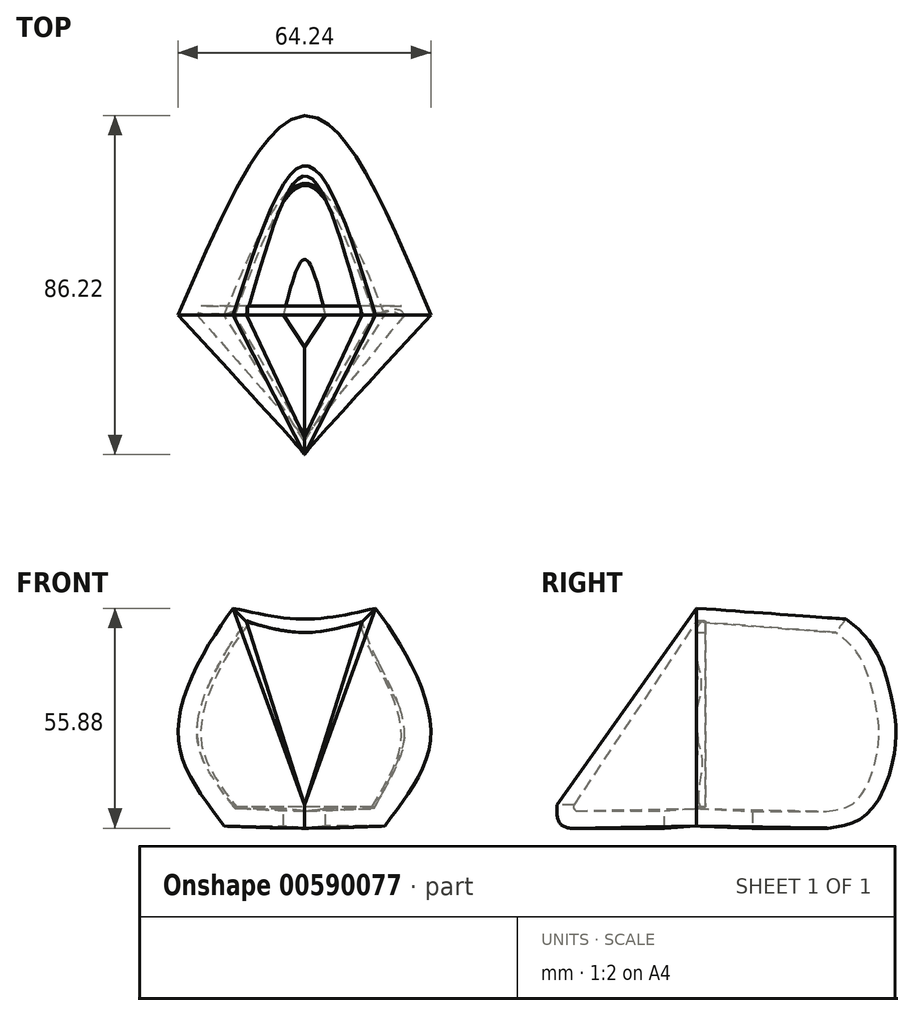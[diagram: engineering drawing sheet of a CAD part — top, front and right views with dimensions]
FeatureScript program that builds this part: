
annotation { "Feature Type Name" : "Feature", "Feature Type Description" : "" }
export const myFeature = defineFeature(function(context is Context, id is Id, definition is map)
    precondition{}
    {
        {
            var Q0;
            Q0=qCreatedBy(makeId("Right.planeOp"),FACE);
            var sketch = newSketch(context, id + "F0", { "sketchPlane" : qUnion([Q0])});
            skLineSegment(sketch, "E0", {"start": v(0, 0) * mm, "end": v(0, 26.93) * mm, "construction": true});
            skLineSegment(sketch, "E1", {"start": v(14.1, 0) * mm, "end": v(33.38, 0) * mm});
            skFitSpline(sketch, "E2", {"points": [v(33.38, 0) * mm, v(40.37, 1.65) * mm, v(46.58, 7.95) * mm, v(50.49, 20.86) * mm, v(49.98, 30.7) * mm, v(45.22, 45.65) * mm, v(37.92, 53.12) * mm], "startDerivative": vector(53.03, 6.53) * mm, "endDerivative": vector(-48.37, 37.27) * mm});
            skFitSpline(sketch, "E3.0", {"points": [v(32.85, 4.29) * mm, v(33.4, 4.35) * mm, v(34.46, 4.48) * mm, v(35.88, 4.71) * mm, v(37.12, 5) * mm, v(38, 5.3) * mm, v(38.61, 5.59) * mm, v(39.07, 5.84) * mm, v(39.52, 6.14) * mm, v(40.13, 6.6) * mm, v(40.88, 7.31) * mm, v(41.78, 8.39) * mm, v(42.5, 9.48) * mm, v(43.05, 10.48) * mm, v(43.58, 11.59) * mm, v(44.22, 13.11) * mm, v(44.89, 15.1) * mm, v(45.45, 17.14) * mm, v(45.88, 19.16) * mm, v(46.13, 20.75) * mm, v(46.26, 21.92) * mm, v(46.35, 23.02) * mm, v(46.38, 24.3) * mm, v(46.3, 25.84) * mm, v(46.13, 27.48) * mm, v(45.9, 29) * mm, v(45.65, 30.36) * mm, v(45.38, 31.8) * mm, v(44.82, 34.41) * mm, v(44, 37.52) * mm, v(43.12, 40.03) * mm, v(42.57, 41.35) * mm, v(42.15, 42.27) * mm, v(41.71, 43.1) * mm, v(41.28, 43.84) * mm, v(40.81, 44.53) * mm, v(40.16, 45.38) * mm, v(39.28, 46.36) * mm, v(37.7, 47.84) * mm, v(36.3, 48.92) * mm, v(35.28, 49.7) * mm]});
            skLineSegment(sketch, "E4", {"start": v(35.28, 49.7) * mm, "end": v(37.92, 53.12) * mm});
            skLineSegment(sketch, "E5", {"start": v(32.9, 4.3) * mm, "end": v(14.1, 4.3) * mm});
            skLineSegment(sketch, "E6", {"start": v(14.1, 0) * mm, "end": v(14.1, 4.3) * mm});
            skSolve(sketch);
        }
        {
            var Q0;
            Q0=qCreatedBy(makeId("Front.planeOp"),FACE);
            var sketch = newSketch(context, id + "F1", { "sketchPlane" : qUnion([Q0])});
            skLineSegment(sketch, "E7", {"start": v(-17.7, 4.97) * mm, "end": v(-5.36, 4.97) * mm});
            skLineSegment(sketch, "E8", {"start": v(-20.45, 0.52) * mm, "end": v(-5.36, 0.52) * mm});
            skLineSegment(sketch, "E9", {"start": v(-5.36, 0.52) * mm, "end": v(-5.36, 4.97) * mm});
            skFitSpline(sketch, "E10", {"points": [v(-20.45, 0.52) * mm, v(-32.12, 24.06) * mm, v(-18.1, 55.88) * mm], "startDerivative": vector(-32.93, 46.47) * mm, "endDerivative": vector(34.01, 45.62) * mm});
            skFitSpline(sketch, "E11.0", {"points": [v(-16.51, 3.31) * mm, v(-17.95, 5.34) * mm, v(-20.15, 8.25) * mm, v(-22.78, 12.01) * mm, v(-24.49, 14.79) * mm, v(-25.85, 17.52) * mm, v(-26.64, 19.76) * mm, v(-27.05, 21.56) * mm, v(-27.21, 22.69) * mm, v(-27.28, 23.6) * mm, v(-27.3, 24.3) * mm, v(-27.29, 25.02) * mm, v(-27.23, 26.01) * mm, v(-27.07, 27.32) * mm, v(-26.65, 29.52) * mm, v(-25.82, 32.43) * mm, v(-24.4, 36.08) * mm, v(-22.06, 41) * mm, v(-18.52, 47) * mm, v(-15.59, 51.17) * mm, v(-14.23, 53) * mm]});
            skLineSegment(sketch, "E12", {"start": v(-18.1, 55.88) * mm, "end": v(-14.66, 52.41) * mm});
            skLineSegment(sketch, "E13.MirrorCS", {"start": v(17.7, 4.97) * mm, "end": v(5.36, 4.97) * mm});
            skLineSegment(sketch, "E14.MirrorCS", {"start": v(20.45, 0.52) * mm, "end": v(5.36, 0.52) * mm});
            skFitSpline(sketch, "E15.MirrorCS", {"points": [v(20.45, 0.52) * mm, v(32.12, 24.06) * mm, v(18.1, 55.88) * mm], "startDerivative": vector(32.93, 46.47) * mm, "endDerivative": vector(-34.01, 45.62) * mm});
            skLineSegment(sketch, "E16.MirrorCS", {"start": v(18.1, 55.88) * mm, "end": v(14.66, 52.41) * mm});
            skLineSegment(sketch, "E17.MirrorCS", {"start": v(5.36, 0.52) * mm, "end": v(5.36, 4.97) * mm});
            skFitSpline(sketch, "E18", {"points": [v(17.7, 4.97) * mm, v(21.14, 11.3) * mm, v(25.22, 21.15) * mm, v(23.52, 32.53) * mm, v(17.7, 44.42) * mm, v(14.66, 52.41) * mm], "startDerivative": vector(19, 35.34) * mm, "endDerivative": vector(-13.78, 41.56) * mm});
            skSolve(sketch);
        }
        {
            var Q0;
            Q0=qCreatedBy(makeId("Right.planeOp"),FACE);
            var sketch = newSketch(context, id + "F2", { "sketchPlane" : qUnion([Q0])});
            skLineSegment(sketch, "E19", {"start": v(-8.23, 0) * mm, "end": v(-32.12, 0) * mm});
            skFitSpline(sketch, "E20", {"points": [v(-32.12, 0) * mm, v(-34.22, 0.72) * mm, v(-35.36, 2.7) * mm, v(-35.48, 5.94) * mm], "startDerivative": vector(-7.4, 1.41) * mm, "endDerivative": vector(0.4, 9.03) * mm});
            skLineSegment(sketch, "E21", {"start": v(-8.23, 0) * mm, "end": v(-8.23, 4.44) * mm});
            skLineSegment(sketch, "E22", {"start": v(-30.68, 4.44) * mm, "end": v(-8.23, 4.44) * mm});
            skFitSpline(sketch, "E23", {"points": [v(-30.68, 4.44) * mm, v(-31.16, 5.1) * mm, v(-31.1, 5.94) * mm], "startDerivative": vector(-1.24, 1.25) * mm, "endDerivative": vector(0.4, 1.75) * mm});
            skLineSegment(sketch, "E24", {"start": v(-31.1, 5.94) * mm, "end": v(-35.48, 5.94) * mm});
            skSolve(sketch);
        }
        {
            var Q0;
            Q0=makeQuery(id+"F2.imprint","IMPRINT",FACE,{"disambiguationData":[TD([[makeQuery(id+"F2.imprint","IMPRINT",EDGE,{"derivedFrom":sQuery(id+"F2.wireOp",EDGE,"E19")}),-1.0]])]});
            var Q1;
            Q1=makeQuery(id+"F1.imprint","IMPRINT",FACE,{"disambiguationData":[TD([[makeQuery(id+"F1.imprint","IMPRINT",EDGE,{"derivedFrom":sQuery(id+"F1.wireOp",EDGE,"E13.MirrorCS")}),1.0]])]});
            loft(context, id + "F3", {"sheetProfilesArray" : [{ "sheetProfileEntities" : qUnion([Q0]) }, { "sheetProfileEntities" : qUnion([Q1]) }]});
        }
        {
            var Q1;
            Q1=makeQuery(id+"F3.opLoft","CAP_FACE",FACE,{"disambiguationData":[OSD([makeQuery(id+"F2.imprint","IMPRINT",FACE,{"disambiguationData":[TD([[makeQuery(id+"F2.imprint","IMPRINT",EDGE,{"derivedFrom":sQuery(id+"F2.wireOp",EDGE,"E19")}),-1.0]])]})])],"isStart":true});
            var Q2;
            Q2=makeQuery(id+"F1.imprint","IMPRINT",FACE,{"disambiguationData":[TD([[makeQuery(id+"F1.imprint","IMPRINT",EDGE,{"derivedFrom":sQuery(id+"F1.wireOp",EDGE,"E8")}),1.0]])]});
            loft(context, id + "F4", {"operationType" : NewBodyOperationType.ADD, "sheetProfilesArray" : [{ "sheetProfileEntities" : qUnion([Q1]) }, { "sheetProfileEntities" : qUnion([Q2]) }]});
        }
        {
            var Q1;
            Q1=makeQuery(id+"F1.imprint","IMPRINT",FACE,{"disambiguationData":[TD([[makeQuery(id+"F1.imprint","IMPRINT",EDGE,{"derivedFrom":sQuery(id+"F1.wireOp",EDGE,"E13.MirrorCS")}),1.0]])]});
            var Q2;
            Q2=makeQuery(id+"F0.imprint","IMPRINT",FACE,{"disambiguationData":[TD([[makeQuery(id+"F0.imprint","IMPRINT",EDGE,{"derivedFrom":sQuery(id+"F0.wireOp",EDGE,"E1")}),1.0]])]});
            var Q3;
            Q3=makeQuery(id+"F1.imprint","IMPRINT",FACE,{"disambiguationData":[TD([[makeQuery(id+"F1.imprint","IMPRINT",EDGE,{"derivedFrom":sQuery(id+"F1.wireOp",EDGE,"E8")}),1.0]])]});
            loft(context, id + "F5", {"operationType" : NewBodyOperationType.ADD, "sheetProfilesArray" : [{ "sheetProfileEntities" : qUnion([Q1]) }, { "sheetProfileEntities" : qUnion([Q2]) }, { "sheetProfileEntities" : qUnion([Q3]) }]});
        }
        {
            var Q0;
            Q0=qCreatedBy(makeId("Front.planeOp"),FACE);
            var sketch = newSketch(context, id + "F6", { "sketchPlane" : qUnion([Q0])});
            skFitSpline(sketch, "E25", {"points": [v(-14.51, 52.7) * mm, v(-10.57, 51.32) * mm, v(-3.9, 49.95) * mm, v(2.35, 49.78) * mm, v(8.43, 50.81) * mm, v(13.05, 51.92) * mm, v(14.34, 52.35) * mm], "startDerivative": vector(23.05, -8.87) * mm, "endDerivative": vector(12.03, 4.43) * mm});
            skFitSpline(sketch, "E26", {"points": [v(14.34, 52.35) * mm, v(15.1, 51) * mm, v(19.8, 39.84) * mm, v(23.83, 31.44) * mm, v(25.53, 24.1) * mm, v(21.6, 12.62) * mm, v(17.77, 5.4) * mm], "startDerivative": vector(8.62, -12.68) * mm, "endDerivative": vector(-21.48, -38.76) * mm});
            skFitSpline(sketch, "E27", {"points": [v(17.77, 5.4) * mm, v(-17.63, 5.4) * mm], "startDerivative": vector(-35.4, 0) * mm, "endDerivative": vector(-35.4, 0) * mm});
            skFitSpline(sketch, "E28", {"points": [v(-17.63, 5.4) * mm, v(-21.24, 9.65) * mm, v(-26.03, 18.15) * mm, v(-26.88, 29) * mm, v(-23.37, 38.14) * mm, v(-18.7, 46.86) * mm, v(-14.51, 52.7) * mm], "startDerivative": vector(-26.14, 28.84) * mm, "endDerivative": vector(27.88, 36.08) * mm});
            skSolve(sketch);
        }
        {
            var Q0;
            Q0=makeQuery(id+"F6.imprint","IMPRINT",FACE,{"disambiguationData":[TD([[makeQuery(id+"F6.imprint","IMPRINT",EDGE,{"derivedFrom":sQuery(id+"F6.wireOp",EDGE,"E25")}),-1.0]])]});
            extrude(context, id + "F7", {"entities" : qUnion([Q0]), "operationType" : NewBodyOperationType.ADD, "oppositeDirection" : true, "depth" : 2.3 * mm, "offsetDistance" : 25.4 * mm});
        }
    });
